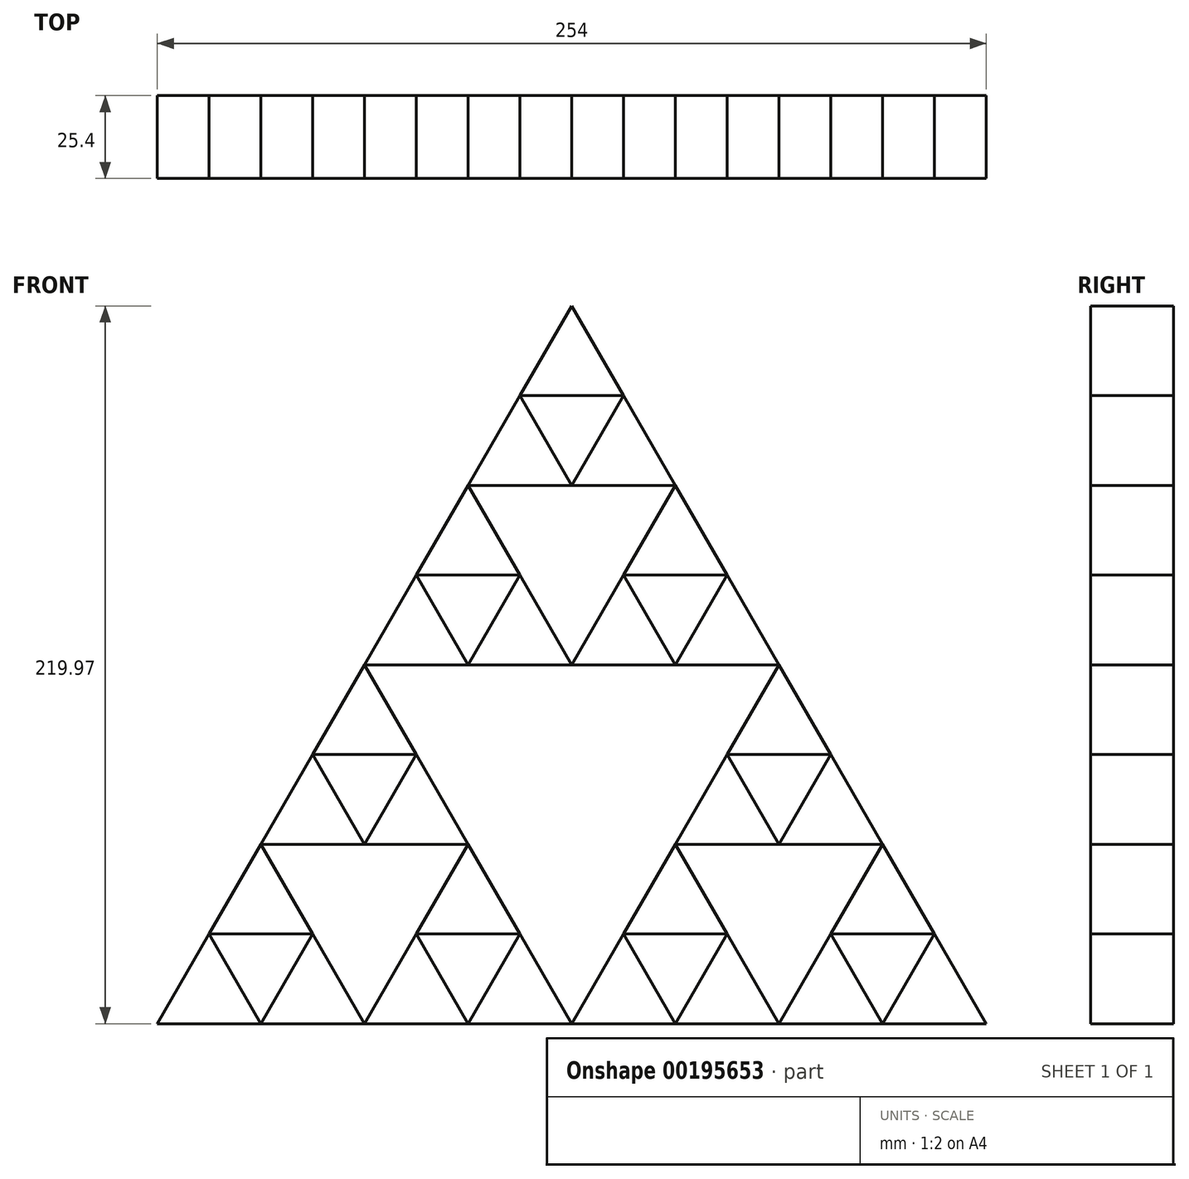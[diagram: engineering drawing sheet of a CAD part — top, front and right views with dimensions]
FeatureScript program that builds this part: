
annotation { "Feature Type Name" : "Feature", "Feature Type Description" : "" }
export const myFeature = defineFeature(function(context is Context, id is Id, definition is map)
    precondition{}
    {
        {
            var Q0;
            Q0=qCreatedBy(makeId("Front.planeOp"),FACE);
            var sketch = newSketch(context, id + "F0", { "sketchPlane" : qUnion([Q0])});
            skLineSegment(sketch, "E0", {"start": v(0, 0) * mm, "end": v(-127, -219.97) * mm});
            skLineSegment(sketch, "E1", {"start": v(-127, -219.97) * mm, "end": v(127, -219.97) * mm});
            skLineSegment(sketch, "E2", {"start": v(127, -219.97) * mm, "end": v(0, 0) * mm});
            skLineSegment(sketch, "E3", {"start": v(-63.5, -109.99) * mm, "end": v(63.5, -109.99) * mm});
            skLineSegment(sketch, "E4", {"start": v(63.5, -109.99) * mm, "end": v(0, -219.97) * mm});
            skLineSegment(sketch, "E5", {"start": v(0, -219.97) * mm, "end": v(-63.5, -109.99) * mm});
            skPoint(sketch, "E6", {"position": v(0, 0) * mm});
            skLineSegment(sketch, "E7", {"start": v(-63.5, -219.97) * mm, "end": v(-31.75, -164.98) * mm});
            skLineSegment(sketch, "E8", {"start": v(-31.75, -164.98) * mm, "end": v(-95.25, -164.98) * mm});
            skLineSegment(sketch, "E9", {"start": v(-95.25, -164.98) * mm, "end": v(-63.5, -219.97) * mm});
            skLineSegment(sketch, "E10", {"start": v(31.75, -164.98) * mm, "end": v(95.25, -164.98) * mm});
            skLineSegment(sketch, "E11", {"start": v(95.25, -164.98) * mm, "end": v(63.5, -219.97) * mm});
            skLineSegment(sketch, "E12", {"start": v(63.5, -219.97) * mm, "end": v(31.75, -164.98) * mm});
            skLineSegment(sketch, "E13", {"start": v(0, -109.99) * mm, "end": v(31.75, -55) * mm});
            skLineSegment(sketch, "E14", {"start": v(31.75, -55) * mm, "end": v(-31.75, -55) * mm});
            skLineSegment(sketch, "E15", {"start": v(-31.75, -55) * mm, "end": v(0, -109.99) * mm});
            skLineSegment(sketch, "E16", {"start": v(0, -55) * mm, "end": v(-15.87, -27.5) * mm});
            skLineSegment(sketch, "E17", {"start": v(-15.87, -27.5) * mm, "end": v(15.87, -27.5) * mm});
            skLineSegment(sketch, "E18", {"start": v(15.87, -27.5) * mm, "end": v(0, -55) * mm});
            skLineSegment(sketch, "E19", {"start": v(15.87, -82.49) * mm, "end": v(47.62, -82.49) * mm});
            skLineSegment(sketch, "E20", {"start": v(47.62, -82.49) * mm, "end": v(31.75, -109.99) * mm});
            skLineSegment(sketch, "E21", {"start": v(31.75, -109.99) * mm, "end": v(15.88, -82.49) * mm});
            skLineSegment(sketch, "E22", {"start": v(-47.62, -82.49) * mm, "end": v(-15.87, -82.49) * mm});
            skLineSegment(sketch, "E23", {"start": v(-15.87, -82.49) * mm, "end": v(-31.75, -109.99) * mm});
            skLineSegment(sketch, "E24", {"start": v(-31.75, -109.99) * mm, "end": v(-47.62, -82.49) * mm});
            skLineSegment(sketch, "E25", {"start": v(-63.5, -164.98) * mm, "end": v(-47.62, -137.48) * mm});
            skLineSegment(sketch, "E26", {"start": v(-47.62, -137.48) * mm, "end": v(-79.37, -137.48) * mm});
            skLineSegment(sketch, "E27", {"start": v(-79.38, -137.48) * mm, "end": v(-63.5, -164.98) * mm});
            skLineSegment(sketch, "E28", {"start": v(-79.37, -192.47) * mm, "end": v(-111.12, -192.47) * mm});
            skLineSegment(sketch, "E29", {"start": v(-111.12, -192.47) * mm, "end": v(-95.25, -219.97) * mm});
            skLineSegment(sketch, "E30", {"start": v(-95.25, -219.97) * mm, "end": v(-79.37, -192.47) * mm});
            skLineSegment(sketch, "E31", {"start": v(63.5, -164.98) * mm, "end": v(79.38, -137.48) * mm});
            skLineSegment(sketch, "E32", {"start": v(79.38, -137.48) * mm, "end": v(47.62, -137.48) * mm});
            skLineSegment(sketch, "E33", {"start": v(47.62, -137.48) * mm, "end": v(63.5, -164.98) * mm});
            skLineSegment(sketch, "E34", {"start": v(47.63, -192.47) * mm, "end": v(31.75, -219.97) * mm});
            skLineSegment(sketch, "E35", {"start": v(31.75, -219.97) * mm, "end": v(15.88, -192.47) * mm});
            skLineSegment(sketch, "E36", {"start": v(15.88, -192.47) * mm, "end": v(47.63, -192.47) * mm});
            skLineSegment(sketch, "E37", {"start": v(79.38, -192.47) * mm, "end": v(111.13, -192.47) * mm});
            skLineSegment(sketch, "E38", {"start": v(111.13, -192.47) * mm, "end": v(95.25, -219.97) * mm});
            skLineSegment(sketch, "E39", {"start": v(95.25, -219.97) * mm, "end": v(79.38, -192.47) * mm});
            skLineSegment(sketch, "E40", {"start": v(-47.62, -192.47) * mm, "end": v(-15.87, -192.47) * mm});
            skLineSegment(sketch, "E41", {"start": v(-15.87, -192.47) * mm, "end": v(-31.75, -219.97) * mm});
            skLineSegment(sketch, "E42", {"start": v(-31.75, -219.97) * mm, "end": v(-47.62, -192.47) * mm});
            skSolve(sketch);
        }
        {
            var Q0;
            {var subQ3=sQuery(id+"F0.wireOp",EDGE,"E17");Q0=makeQuery(id+"F0.imprint","IMPRINT",FACE,{"disambiguationData":[TD([[makeQuery(id+"F0.imprint","IMPRINT",EDGE,{"derivedFrom":subQ3}),1.0]])]});}
            var Q1;
            {var subQ3=sQuery(id+"F0.wireOp",EDGE,"E16");Q1=makeQuery(id+"F0.imprint","IMPRINT",FACE,{"disambiguationData":[TD([[makeQuery(id+"F0.imprint","IMPRINT",EDGE,{"derivedFrom":subQ3}),1.0]])]});}
            var Q2;
            {var subQ3=sQuery(id+"F0.wireOp",EDGE,"E18");Q2=makeQuery(id+"F0.imprint","IMPRINT",FACE,{"disambiguationData":[TD([[makeQuery(id+"F0.imprint","IMPRINT",EDGE,{"derivedFrom":subQ3}),1.0]])]});}
            var Q3;
            {var subQ3=sQuery(id+"F0.wireOp",EDGE,"E22");Q3=makeQuery(id+"F0.imprint","IMPRINT",FACE,{"disambiguationData":[TD([[makeQuery(id+"F0.imprint","IMPRINT",EDGE,{"derivedFrom":subQ3}),1.0]])]});}
            var Q4;
            {var subQ3=sQuery(id+"F0.wireOp",EDGE,"E24");Q4=makeQuery(id+"F0.imprint","IMPRINT",FACE,{"disambiguationData":[TD([[makeQuery(id+"F0.imprint","IMPRINT",EDGE,{"derivedFrom":subQ3}),1.0]])]});}
            var Q5;
            {var subQ3=sQuery(id+"F0.wireOp",EDGE,"E23");Q5=makeQuery(id+"F0.imprint","IMPRINT",FACE,{"disambiguationData":[TD([[makeQuery(id+"F0.imprint","IMPRINT",EDGE,{"derivedFrom":subQ3}),1.0]])]});}
            var Q6;
            {var subQ3=sQuery(id+"F0.wireOp",EDGE,"E21");Q6=makeQuery(id+"F0.imprint","IMPRINT",FACE,{"disambiguationData":[TD([[makeQuery(id+"F0.imprint","IMPRINT",EDGE,{"derivedFrom":subQ3}),1.0]])]});}
            var Q7;
            {var subQ3=sQuery(id+"F0.wireOp",EDGE,"E19");Q7=makeQuery(id+"F0.imprint","IMPRINT",FACE,{"disambiguationData":[TD([[makeQuery(id+"F0.imprint","IMPRINT",EDGE,{"derivedFrom":subQ3}),1.0]])]});}
            var Q8;
            {var subQ3=sQuery(id+"F0.wireOp",EDGE,"E20");Q8=makeQuery(id+"F0.imprint","IMPRINT",FACE,{"disambiguationData":[TD([[makeQuery(id+"F0.imprint","IMPRINT",EDGE,{"derivedFrom":subQ3}),1.0]])]});}
            var Q9;
            {var subQ3=sQuery(id+"F0.wireOp",EDGE,"E32");Q9=makeQuery(id+"F0.imprint","IMPRINT",FACE,{"disambiguationData":[TD([[makeQuery(id+"F0.imprint","IMPRINT",EDGE,{"derivedFrom":subQ3}),-1.0]])]});}
            var Q10;
            {var subQ3=sQuery(id+"F0.wireOp",EDGE,"E33");Q10=makeQuery(id+"F0.imprint","IMPRINT",FACE,{"disambiguationData":[TD([[makeQuery(id+"F0.imprint","IMPRINT",EDGE,{"derivedFrom":subQ3}),-1.0]])]});}
            var Q11;
            {var subQ3=sQuery(id+"F0.wireOp",EDGE,"E31");Q11=makeQuery(id+"F0.imprint","IMPRINT",FACE,{"disambiguationData":[TD([[makeQuery(id+"F0.imprint","IMPRINT",EDGE,{"derivedFrom":subQ3}),-1.0]])]});}
            var Q12;
            {var subQ3=sQuery(id+"F0.wireOp",EDGE,"E37");Q12=makeQuery(id+"F0.imprint","IMPRINT",FACE,{"disambiguationData":[TD([[makeQuery(id+"F0.imprint","IMPRINT",EDGE,{"derivedFrom":subQ3}),1.0]])]});}
            var Q13;
            {var subQ3=sQuery(id+"F0.wireOp",EDGE,"E39");Q13=makeQuery(id+"F0.imprint","IMPRINT",FACE,{"disambiguationData":[TD([[makeQuery(id+"F0.imprint","IMPRINT",EDGE,{"derivedFrom":subQ3}),1.0]])]});}
            var Q14;
            {var subQ3=sQuery(id+"F0.wireOp",EDGE,"E38");Q14=makeQuery(id+"F0.imprint","IMPRINT",FACE,{"disambiguationData":[TD([[makeQuery(id+"F0.imprint","IMPRINT",EDGE,{"derivedFrom":subQ3}),1.0]])]});}
            var Q15;
            {var subQ3=sQuery(id+"F0.wireOp",EDGE,"E36");Q15=makeQuery(id+"F0.imprint","IMPRINT",FACE,{"disambiguationData":[TD([[makeQuery(id+"F0.imprint","IMPRINT",EDGE,{"derivedFrom":subQ3}),1.0]])]});}
            var Q16;
            {var subQ3=sQuery(id+"F0.wireOp",EDGE,"E34");Q16=makeQuery(id+"F0.imprint","IMPRINT",FACE,{"disambiguationData":[TD([[makeQuery(id+"F0.imprint","IMPRINT",EDGE,{"derivedFrom":subQ3}),1.0]])]});}
            var Q17;
            {var subQ3=sQuery(id+"F0.wireOp",EDGE,"E35");Q17=makeQuery(id+"F0.imprint","IMPRINT",FACE,{"disambiguationData":[TD([[makeQuery(id+"F0.imprint","IMPRINT",EDGE,{"derivedFrom":subQ3}),1.0]])]});}
            var Q18;
            {var subQ3=sQuery(id+"F0.wireOp",EDGE,"E41");Q18=makeQuery(id+"F0.imprint","IMPRINT",FACE,{"disambiguationData":[TD([[makeQuery(id+"F0.imprint","IMPRINT",EDGE,{"derivedFrom":subQ3}),1.0]])]});}
            var Q19;
            {var subQ3=sQuery(id+"F0.wireOp",EDGE,"E40");Q19=makeQuery(id+"F0.imprint","IMPRINT",FACE,{"disambiguationData":[TD([[makeQuery(id+"F0.imprint","IMPRINT",EDGE,{"derivedFrom":subQ3}),1.0]])]});}
            var Q20;
            {var subQ3=sQuery(id+"F0.wireOp",EDGE,"E42");Q20=makeQuery(id+"F0.imprint","IMPRINT",FACE,{"disambiguationData":[TD([[makeQuery(id+"F0.imprint","IMPRINT",EDGE,{"derivedFrom":subQ3}),1.0]])]});}
            var Q21;
            {var subQ3=sQuery(id+"F0.wireOp",EDGE,"E30");Q21=makeQuery(id+"F0.imprint","IMPRINT",FACE,{"disambiguationData":[TD([[makeQuery(id+"F0.imprint","IMPRINT",EDGE,{"derivedFrom":subQ3}),-1.0]])]});}
            var Q22;
            {var subQ3=sQuery(id+"F0.wireOp",EDGE,"E29");Q22=makeQuery(id+"F0.imprint","IMPRINT",FACE,{"disambiguationData":[TD([[makeQuery(id+"F0.imprint","IMPRINT",EDGE,{"derivedFrom":subQ3}),-1.0]])]});}
            var Q23;
            {var subQ3=sQuery(id+"F0.wireOp",EDGE,"E28");Q23=makeQuery(id+"F0.imprint","IMPRINT",FACE,{"disambiguationData":[TD([[makeQuery(id+"F0.imprint","IMPRINT",EDGE,{"derivedFrom":subQ3}),-1.0]])]});}
            var Q24;
            {var subQ3=sQuery(id+"F0.wireOp",EDGE,"E27");Q24=makeQuery(id+"F0.imprint","IMPRINT",FACE,{"disambiguationData":[TD([[makeQuery(id+"F0.imprint","IMPRINT",EDGE,{"derivedFrom":subQ3}),-1.0]])]});}
            var Q25;
            {var subQ3=sQuery(id+"F0.wireOp",EDGE,"E25");Q25=makeQuery(id+"F0.imprint","IMPRINT",FACE,{"disambiguationData":[TD([[makeQuery(id+"F0.imprint","IMPRINT",EDGE,{"derivedFrom":subQ3}),-1.0]])]});}
            var Q26;
            {var subQ3=sQuery(id+"F0.wireOp",EDGE,"E26");Q26=makeQuery(id+"F0.imprint","IMPRINT",FACE,{"disambiguationData":[TD([[makeQuery(id+"F0.imprint","IMPRINT",EDGE,{"derivedFrom":subQ3}),-1.0]])]});}
            extrude(context, id + "F1", {"entities" : qUnion([Q0, Q1, Q2, Q3, Q4, Q5, Q6, Q7, Q8, Q9, Q10, Q11, Q12, Q13, Q14, Q15, Q16, Q17, Q18, Q19, Q20, Q21, Q22, Q23, Q24, Q25, Q26]), "depth" : 25.4 * mm});
        }
    });
